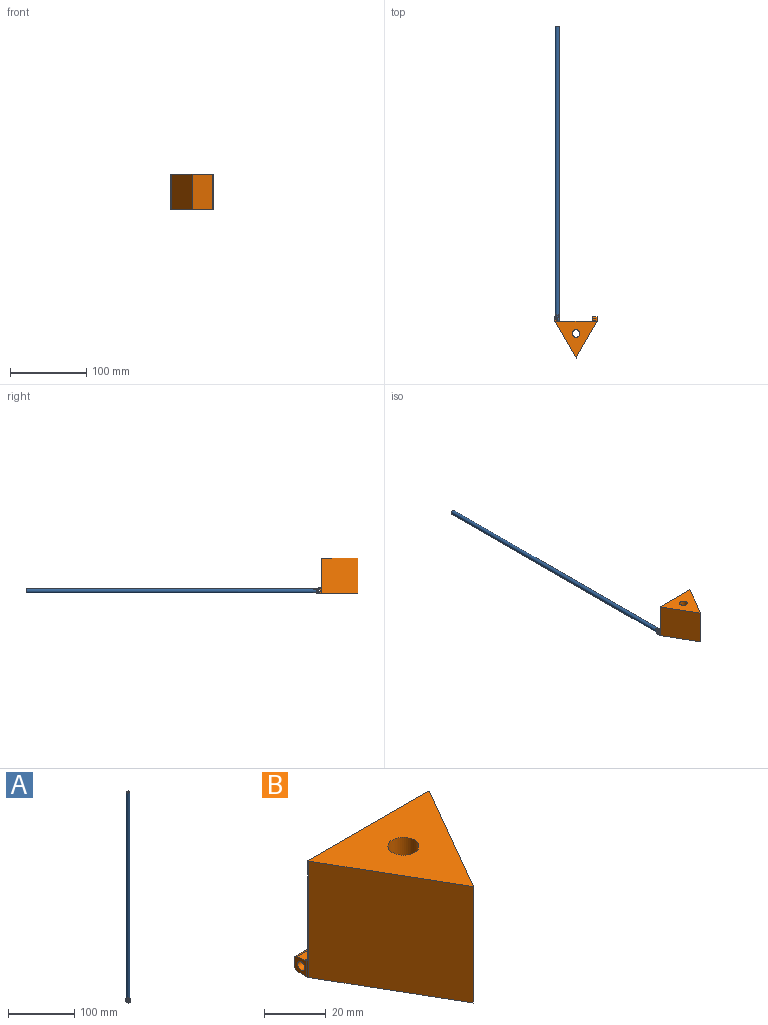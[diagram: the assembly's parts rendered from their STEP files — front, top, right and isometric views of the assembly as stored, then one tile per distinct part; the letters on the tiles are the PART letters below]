
ASSEMBLY  parts=2 mates=1
PART A: 46 faces, bbox 12.5x8.7x389.4 mm
  f0: cylinder r=2.5mm len=5mm, axis (-1,0,0), area 2.6mm2, adj f5,f13,f45
  f1: cylinder r=1.6mm len=381mm, axis (0,0,-1), area 3830.2mm2, adj f3,f8
  f2: cylinder r=2.8mm len=381.9mm, axis (0,0,-1), area 6693.4mm2, adj f3,f15,f16,f17,f18,f19,f20,f22
  f3: plane 5.6x5.6mm, normal (0,0,1), area 16.6mm2, adj f1,f2
  f4: cylinder r=2.5mm len=5mm, axis (-1,0,0), area 2.6mm2, adj f6,f10,f45
  f5: plane 6.05x5.91mm, normal (-1,0,0), area 7.3mm2, adj f0,f12,f14,f23,f25,f33,f34,f35
  f6: plane 6.05x5.91mm, normal (1,0,0), area 7.3mm2, adj f4,f9,f11,f21,f28,f40,f41,f42
  f7: cylinder r=4mm len=8mm, axis (-1,0,0), area 33.6mm2, adj f29,f30,f34,f41
  f8: cylinder r=4mm len=3.2mm, axis (-1,0,0), area 8.2mm2, adj f1
  f9: cylinder r=0.5mm len=0.32mm, axis (0,1,0), area 0.1mm2, adj f6,f10,f18
  f10: bspline ~2.76x0.61mm, area 0.6mm2, adj f4,f9,f11,f19
  f11: cylinder r=0.5mm len=0.32mm, axis (0,1,0), area 0.1mm2, adj f6,f10,f20
  f12: cylinder r=0.5mm len=0.32mm, axis (0,-1,0), area 0.1mm2, adj f5,f13,f17
  f13: bspline ~2.38x0.44mm, area 0.6mm2, adj f0,f12,f14,f16
  f14: cylinder r=0.5mm len=0.32mm, axis (0,-1,0), area 0.1mm2, adj f5,f13,f15
  f15: bspline ~1.34x1.28mm, area 0.3mm2, adj f2,f14,f16,f23
  f16: bspline ~3.83x1.07mm, area 3.5mm2, adj f2,f13,f15,f17
  f17: bspline ~1.22x1.19mm, area 0.3mm2, adj f2,f12,f16,f25
  f18: bspline ~1.34x1.28mm, area 0.3mm2, adj f2,f9,f19,f21
  f19: bspline ~3.83x1.07mm, area 3.5mm2, adj f2,f10,f18,f20
  f20: bspline ~1.22x1.19mm, area 0.3mm2, adj f2,f11,f19,f28
  f21: bspline ~1.18x0.5mm, area 0mm2, adj f6,f18,f22,f39
  f22: cylinder r=0.1mm len=4.11mm, axis (0,0,-1), area 0.1mm2, adj f2,f21,f38
  f23: bspline ~1.18x0.5mm, area 0mm2, adj f5,f15,f24,f37
  f24: cylinder r=0.1mm len=4.11mm, axis (0,0,-1), area 0.1mm2, adj f2,f23,f36
  f25: bspline ~1.07x0.5mm, area 0mm2, adj f5,f17,f26,f32
  f26: cylinder r=0.1mm len=4.11mm, axis (0,0,-1), area 0.1mm2, adj f2,f25,f31
  f27: cylinder r=0.1mm len=4.11mm, axis (0,0,-1), area 0.1mm2, adj f2,f28,f44
  f28: bspline ~1.09x0.5mm, area 0mm2, adj f6,f20,f27,f43
  f29: bspline ~12.46x5.7mm, area 8.4mm2, adj f2,f7,f35,f36,f37,f42,f43,f44
  f30: bspline ~12.46x5.7mm, area 8.4mm2, adj f2,f7,f31,f32,f33,f38,f39,f40
  f31: bspline ~4.39x1mm, area 1.8mm2, adj f26,f30,f32
  f32: bspline ~0.98x0.95mm, area 0.3mm2, adj f25,f30,f31,f33
  f33: bspline ~3.63x2.46mm, area 2mm2, adj f5,f30,f32,f34
  f34: torus R=3mm, axis (1,0,0), area 24.1mm2, adj f5,f7,f33,f35
  f35: bspline ~3.61x2.45mm, area 2mm2, adj f5,f29,f34,f37
  f36: bspline ~4.23x0.95mm, area 1.8mm2, adj f24,f29,f37
  f37: bspline ~1.12x1.08mm, area 0.3mm2, adj f23,f29,f35,f36
  f38: bspline ~4.23x0.95mm, area 1.8mm2, adj f22,f30,f39
  f39: bspline ~1.12x1.08mm, area 0.3mm2, adj f21,f30,f38,f40
  f40: bspline ~3.63x2.46mm, area 2mm2, adj f6,f30,f39,f41
  f41: torus R=3mm, axis (1,0,0), area 24.1mm2, adj f6,f7,f40,f42
  f42: bspline ~3.61x2.45mm, area 2mm2, adj f6,f29,f41,f43
  f43: bspline ~0.98x0.95mm, area 0.3mm2, adj f28,f29,f42,f44
  f44: bspline ~4.39x1mm, area 1.8mm2, adj f27,f29,f43
  f45: sphere r=3.1mm, area 28.1mm2, adj f0,f4
PART B: 30 faces, bbox 55.4x54x46 mm
  f0: plane 55.32x46mm, normal (0,1,0), area 2432.9mm2, adj f4,f5,f16,f17,f18,f19,f20,f23
  f1: plane 47.65x46mm, normal (-0.87,-0.5,0), area 2531.1mm2, adj f2,f4,f5,f23
  f2: plane 47.65x46mm, normal (0.87,-0.5,0), area 2531.1mm2, adj f1,f4,f5,f18
  f3: cylinder r=5mm len=46mm, axis (0,0,1), area 1445.1mm2, adj f4,f5
  f4: plane 55.43x52.5mm, normal (0,0,-1), area 1306.6mm2, adj f0,f1,f2,f3,f7,f8,f11,f12
  f5: plane 55.32x48mm, normal (0,0,1), area 1251.7mm2, adj f0,f1,f2,f3,f18,f23
  f6: plane 6x3mm, normal (0,0,1), area 18mm2, adj f7,f8,f25,f29
  f7: plane 6x4.5mm, normal (1,0,0), area 18.1mm2, adj f4,f6,f9,f15,f24,f27,f28,f29
  f8: plane 6.48x5.6mm, normal (-1,0,0), area 24.7mm2, adj f4,f6,f9,f15,f23,f25,f28,f29
  f9: plane 6x3mm, normal (0,1,0), area 18mm2, adj f7,f8,f28,f29
  f10: plane 6x3mm, normal (0,0,1), area 18mm2, adj f11,f12,f20,f22
  f11: plane 6.48x5.6mm, normal (1,0,0), area 24.7mm2, adj f4,f10,f13,f14,f18,f20,f21,f22
  f12: plane 6x4.5mm, normal (-1,0,0), area 18.1mm2, adj f4,f10,f13,f14,f16,f19,f21,f22
  f13: plane 6x3mm, normal (0,1,0), area 18mm2, adj f11,f12,f21,f22
  f14: cylinder r=1.6mm len=6mm, axis (-1,0,0), area 60.3mm2, adj f11,f12,f17
  f15: cylinder r=1.6mm len=6mm, axis (-1,0,0), area 60.3mm2, adj f7,f8,f26
  f16: cylinder r=1.5mm len=2.44mm, axis (0,0,-1), area 5.8mm2, adj f0,f4,f12,f17
  f17: bspline ~1.58x1.58mm, area 2.5mm2, adj f0,f14,f16,f19
  f18: cylinder r=1.5mm len=46mm, axis (0,0,-1), area 20.3mm2, adj f0,f2,f4,f5,f11,f20
  f19: cylinder r=1.5mm len=3.94mm, axis (0,0,-1), area 7mm2, adj f0,f12,f17,f20
  f20: cylinder r=1.5mm len=7.5mm, axis (-1,0,0), area 15.4mm2, adj f0,f10,f11,f18,f19
  f21: cylinder r=1.5mm len=6mm, axis (-1,0,0), area 14.1mm2, adj f4,f11,f12,f13
  f22: cylinder r=1.5mm len=6mm, axis (-1,0,0), area 14.1mm2, adj f10,f11,f12,f13
  f23: cylinder r=1.5mm len=46mm, axis (0,0,1), area 20.3mm2, adj f0,f1,f4,f5,f8,f25
  f24: cylinder r=1.5mm len=2.44mm, axis (0,0,1), area 5.8mm2, adj f0,f4,f7,f26
  f25: cylinder r=1.5mm len=7.5mm, axis (-1,0,0), area 15.4mm2, adj f0,f6,f8,f23,f27
  f26: bspline ~1.58x1.58mm, area 2.5mm2, adj f0,f15,f24,f27
  f27: cylinder r=1.5mm len=3.94mm, axis (0,0,1), area 7mm2, adj f0,f7,f25,f26
  f28: cylinder r=1.5mm len=6mm, axis (-1,0,0), area 14.1mm2, adj f4,f7,f8,f9
  f29: cylinder r=1.5mm len=6mm, axis (-1,0,0), area 14.1mm2, adj f6,f7,f8,f9
PLACE A rot(axis=(-1,0,0),90deg) t=(-54.53,-8.17,-250.93)mm
PLACE B t=(-29.82,-32.17,-207.93)mm
MATE revolute A.f7 <-> B.f14  axis (-1,0,0) through (-54.53,-13.17,-250.93)mm
